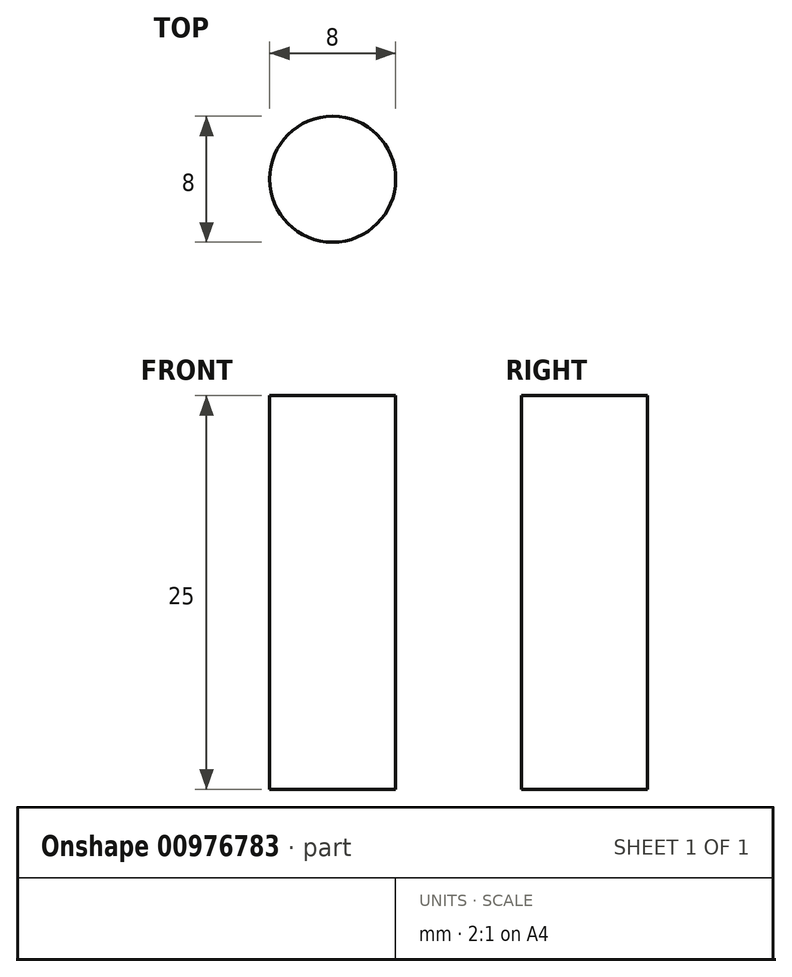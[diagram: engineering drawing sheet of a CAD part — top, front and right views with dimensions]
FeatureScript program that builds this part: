
annotation { "Feature Type Name" : "Feature", "Feature Type Description" : "" }
export const myFeature = defineFeature(function(context is Context, id is Id, definition is map)
    precondition{}
    {
        {
            var Q0;
            Q0=qCreatedBy(makeId("Top.planeOp"),FACE);
            var sketch = newSketch(context, id + "F0", { "sketchPlane" : qUnion([Q0])});
            skCircle(sketch, "E0", {"center": v(0, 0) * mm, "radius": 4 * mm});
            skArc(sketch, "E1", {"start": v(4.61, 14.97) * mm, "mid": v(4.54, 14.95) * mm, "end": v(4.49, 14.9) * mm});
            skArc(sketch, "E2", {"start": v(5.05, 14.83) * mm, "mid": v(4.83, 14.9) * mm, "end": v(4.61, 14.97) * mm});
            skArc(sketch, "E3", {"start": v(5.11, 14.7) * mm, "mid": v(5.1, 14.77) * mm, "end": v(5.05, 14.83) * mm});
            skArc(sketch, "E4", {"start": v(5.1, 14.54) * mm, "mid": v(5.11, 14.62) * mm, "end": v(5.11, 14.7) * mm});
            skArc(sketch, "E5", {"start": v(5.1, 14.54) * mm, "mid": v(5.48, 13.88) * mm, "end": v(6.22, 14.1) * mm});
            skArc(sketch, "E6", {"start": v(6.32, 14.22) * mm, "mid": v(6.27, 14.16) * mm, "end": v(6.22, 14.1) * mm});
            skArc(sketch, "E7", {"start": v(6.45, 14.28) * mm, "mid": v(6.38, 14.26) * mm, "end": v(6.32, 14.22) * mm});
            skArc(sketch, "E8", {"start": v(6.87, 14.08) * mm, "mid": v(6.66, 14.18) * mm, "end": v(6.45, 14.28) * mm});
            skArc(sketch, "E9", {"start": v(6.91, 13.94) * mm, "mid": v(6.9, 14.01) * mm, "end": v(6.87, 14.08) * mm});
            skArc(sketch, "E10", {"start": v(6.89, 13.8) * mm, "mid": v(6.9, 13.86) * mm, "end": v(6.91, 13.94) * mm});
            skArc(sketch, "E11", {"start": v(6.89, 13.8) * mm, "mid": v(7.18, 13.08) * mm, "end": v(7.94, 13.21) * mm});
            skArc(sketch, "E12", {"start": v(8.05, 13.31) * mm, "mid": v(8, 13.27) * mm, "end": v(7.94, 13.21) * mm});
            skArc(sketch, "E13", {"start": v(8.2, 13.36) * mm, "mid": v(8.12, 13.35) * mm, "end": v(8.05, 13.31) * mm});
            skArc(sketch, "E14", {"start": v(8.58, 13.1) * mm, "mid": v(8.39, 13.23) * mm, "end": v(8.2, 13.36) * mm});
            skArc(sketch, "E15", {"start": v(8.6, 12.96) * mm, "mid": v(8.6, 13.04) * mm, "end": v(8.58, 13.1) * mm});
            skArc(sketch, "E16", {"start": v(8.56, 12.82) * mm, "mid": v(8.59, 12.9) * mm, "end": v(8.6, 12.96) * mm});
            skArc(sketch, "E17", {"start": v(8.56, 12.82) * mm, "mid": v(8.76, 12.08) * mm, "end": v(9.53, 12.11) * mm});
            skArc(sketch, "E18", {"start": v(9.66, 12.2) * mm, "mid": v(9.6, 12.16) * mm, "end": v(9.53, 12.11) * mm});
            skArc(sketch, "E19", {"start": v(9.8, 12.22) * mm, "mid": v(9.73, 12.22) * mm, "end": v(9.66, 12.2) * mm});
            skArc(sketch, "E20", {"start": v(10.16, 11.93) * mm, "mid": v(9.98, 12.08) * mm, "end": v(9.8, 12.22) * mm});
            skArc(sketch, "E21", {"start": v(10.16, 11.78) * mm, "mid": v(10.17, 11.86) * mm, "end": v(10.16, 11.93) * mm});
            skArc(sketch, "E22", {"start": v(10.1, 11.64) * mm, "mid": v(10.13, 11.71) * mm, "end": v(10.16, 11.78) * mm});
            skArc(sketch, "E23", {"start": v(10.1, 11.64) * mm, "mid": v(10.2, 10.88) * mm, "end": v(10.98, 10.82) * mm});
            skArc(sketch, "E24", {"start": v(11.1, 10.9) * mm, "mid": v(11.04, 10.86) * mm, "end": v(10.98, 10.82) * mm});
            skArc(sketch, "E25", {"start": v(11.26, 10.9) * mm, "mid": v(11.18, 10.9) * mm, "end": v(11.1, 10.9) * mm});
            skArc(sketch, "E26", {"start": v(11.57, 10.56) * mm, "mid": v(11.42, 10.73) * mm, "end": v(11.26, 10.9) * mm});
            skArc(sketch, "E27", {"start": v(11.56, 10.42) * mm, "mid": v(11.58, 10.49) * mm, "end": v(11.57, 10.56) * mm});
            skArc(sketch, "E28", {"start": v(11.48, 10.29) * mm, "mid": v(11.52, 10.35) * mm, "end": v(11.56, 10.42) * mm});
            skArc(sketch, "E29", {"start": v(11.48, 10.29) * mm, "mid": v(11.5, 9.52) * mm, "end": v(12.24, 9.36) * mm});
            skArc(sketch, "E30", {"start": v(12.39, 9.41) * mm, "mid": v(12.31, 9.4) * mm, "end": v(12.24, 9.36) * mm});
            skArc(sketch, "E31", {"start": v(12.53, 9.4) * mm, "mid": v(12.46, 9.42) * mm, "end": v(12.39, 9.41) * mm});
            skArc(sketch, "E32", {"start": v(12.8, 9.03) * mm, "mid": v(12.67, 9.22) * mm, "end": v(12.53, 9.4) * mm});
            skArc(sketch, "E33", {"start": v(12.77, 8.89) * mm, "mid": v(12.8, 8.95) * mm, "end": v(12.8, 9.03) * mm});
            skArc(sketch, "E34", {"start": v(12.68, 8.77) * mm, "mid": v(12.73, 8.82) * mm, "end": v(12.77, 8.89) * mm});
            skArc(sketch, "E35", {"start": v(12.68, 8.77) * mm, "mid": v(12.6, 8) * mm, "end": v(13.32, 7.75) * mm});
            skArc(sketch, "E36", {"start": v(13.47, 7.79) * mm, "mid": v(13.4, 7.78) * mm, "end": v(13.32, 7.75) * mm});
            skArc(sketch, "E37", {"start": v(13.61, 7.76) * mm, "mid": v(13.54, 7.78) * mm, "end": v(13.47, 7.79) * mm});
            skArc(sketch, "E38", {"start": v(13.84, 7.35) * mm, "mid": v(13.73, 7.56) * mm, "end": v(13.61, 7.76) * mm});
            skArc(sketch, "E39", {"start": v(13.79, 7.22) * mm, "mid": v(13.82, 7.28) * mm, "end": v(13.84, 7.35) * mm});
            skArc(sketch, "E40", {"start": v(13.68, 7.1) * mm, "mid": v(13.73, 7.16) * mm, "end": v(13.79, 7.22) * mm});
            skArc(sketch, "E41", {"start": v(13.68, 7.1) * mm, "mid": v(13.5, 6.36) * mm, "end": v(14.19, 6.02) * mm});
            skArc(sketch, "E42", {"start": v(14.34, 6.04) * mm, "mid": v(14.26, 6.03) * mm, "end": v(14.19, 6.02) * mm});
            skArc(sketch, "E43", {"start": v(14.48, 6) * mm, "mid": v(14.41, 6.03) * mm, "end": v(14.34, 6.04) * mm});
            skArc(sketch, "E44", {"start": v(14.65, 5.56) * mm, "mid": v(14.57, 5.78) * mm, "end": v(14.48, 6) * mm});
            skArc(sketch, "E45", {"start": v(14.58, 5.43) * mm, "mid": v(14.63, 5.49) * mm, "end": v(14.65, 5.56) * mm});
            skArc(sketch, "E46", {"start": v(14.46, 5.34) * mm, "mid": v(14.52, 5.38) * mm, "end": v(14.58, 5.43) * mm});
            skArc(sketch, "E47", {"start": v(14.46, 5.34) * mm, "mid": v(14.19, 4.62) * mm, "end": v(14.83, 4.2) * mm});
            skArc(sketch, "E48", {"start": v(14.98, 4.2) * mm, "mid": v(14.9, 4.2) * mm, "end": v(14.83, 4.2) * mm});
            skArc(sketch, "E49", {"start": v(15.11, 4.13) * mm, "mid": v(15.05, 4.17) * mm, "end": v(14.98, 4.2) * mm});
            skArc(sketch, "E50", {"start": v(15.23, 3.68) * mm, "mid": v(15.17, 3.9) * mm, "end": v(15.11, 4.13) * mm});
            skArc(sketch, "E51", {"start": v(15.15, 3.56) * mm, "mid": v(15.2, 3.61) * mm, "end": v(15.23, 3.68) * mm});
            skArc(sketch, "E52", {"start": v(15.02, 3.48) * mm, "mid": v(15.08, 3.52) * mm, "end": v(15.15, 3.56) * mm});
            skArc(sketch, "E53", {"start": v(15.02, 3.48) * mm, "mid": v(14.65, 2.8) * mm, "end": v(15.24, 2.3) * mm});
            skArc(sketch, "E54", {"start": v(15.4, 2.28) * mm, "mid": v(15.32, 2.3) * mm, "end": v(15.24, 2.3) * mm});
            skArc(sketch, "E55", {"start": v(15.51, 2.2) * mm, "mid": v(15.46, 2.25) * mm, "end": v(15.4, 2.28) * mm});
            skArc(sketch, "E56", {"start": v(15.57, 1.74) * mm, "mid": v(15.54, 1.97) * mm, "end": v(15.51, 2.2) * mm});
            skArc(sketch, "E57", {"start": v(15.47, 1.63) * mm, "mid": v(15.53, 1.68) * mm, "end": v(15.57, 1.74) * mm});
            skArc(sketch, "E58", {"start": v(15.33, 1.57) * mm, "mid": v(15.4, 1.6) * mm, "end": v(15.47, 1.63) * mm});
            skArc(sketch, "E59", {"start": v(15.33, 1.57) * mm, "mid": v(14.89, 0.95) * mm, "end": v(15.4, 0.38) * mm});
            skArc(sketch, "E60", {"start": v(15.56, 0.34) * mm, "mid": v(15.48, 0.36) * mm, "end": v(15.4, 0.38) * mm});
            skArc(sketch, "E61", {"start": v(15.67, 0.24) * mm, "mid": v(15.62, 0.3) * mm, "end": v(15.56, 0.34) * mm});
            skArc(sketch, "E62", {"start": v(15.67, -0.22) * mm, "mid": v(15.67, 0) * mm, "end": v(15.67, 0.24) * mm});
            skArc(sketch, "E63", {"start": v(15.56, -0.32) * mm, "mid": v(15.62, -0.28) * mm, "end": v(15.67, -0.22) * mm});
            skArc(sketch, "E64", {"start": v(15.41, -0.36) * mm, "mid": v(15.48, -0.34) * mm, "end": v(15.56, -0.32) * mm});
            skArc(sketch, "E65", {"start": v(15.41, -0.36) * mm, "mid": v(14.9, -0.93) * mm, "end": v(15.33, -1.56) * mm});
            skArc(sketch, "E66", {"start": v(15.48, -1.62) * mm, "mid": v(15.4, -1.58) * mm, "end": v(15.33, -1.56) * mm});
            skArc(sketch, "E67", {"start": v(15.57, -1.73) * mm, "mid": v(15.53, -1.66) * mm, "end": v(15.48, -1.62) * mm});
            skArc(sketch, "E68", {"start": v(15.52, -2.19) * mm, "mid": v(15.55, -1.96) * mm, "end": v(15.57, -1.73) * mm});
            skArc(sketch, "E69", {"start": v(15.4, -2.27) * mm, "mid": v(15.46, -2.24) * mm, "end": v(15.52, -2.19) * mm});
            skArc(sketch, "E70", {"start": v(15.24, -2.29) * mm, "mid": v(15.32, -2.28) * mm, "end": v(15.4, -2.27) * mm});
            skArc(sketch, "E71", {"start": v(15.24, -2.29) * mm, "mid": v(14.66, -2.79) * mm, "end": v(15.02, -3.47) * mm});
            skArc(sketch, "E72", {"start": v(15.15, -3.54) * mm, "mid": v(15.09, -3.5) * mm, "end": v(15.02, -3.47) * mm});
            skArc(sketch, "E73", {"start": v(15.23, -3.66) * mm, "mid": v(15.2, -3.6) * mm, "end": v(15.15, -3.54) * mm});
            skArc(sketch, "E74", {"start": v(15.12, -4.11) * mm, "mid": v(15.18, -3.89) * mm, "end": v(15.23, -3.66) * mm});
            skArc(sketch, "E75", {"start": v(14.99, -4.18) * mm, "mid": v(15.06, -4.16) * mm, "end": v(15.12, -4.11) * mm});
            skArc(sketch, "E76", {"start": v(14.84, -4.18) * mm, "mid": v(14.91, -4.18) * mm, "end": v(14.99, -4.18) * mm});
            skArc(sketch, "E77", {"start": v(14.84, -4.18) * mm, "mid": v(14.2, -4.6) * mm, "end": v(14.47, -5.32) * mm});
            skArc(sketch, "E78", {"start": v(14.59, -5.41) * mm, "mid": v(14.53, -5.36) * mm, "end": v(14.47, -5.32) * mm});
            skArc(sketch, "E79", {"start": v(14.65, -5.54) * mm, "mid": v(14.63, -5.47) * mm, "end": v(14.59, -5.41) * mm});
            skArc(sketch, "E80", {"start": v(14.48, -5.98) * mm, "mid": v(14.57, -5.76) * mm, "end": v(14.65, -5.54) * mm});
            skArc(sketch, "E81", {"start": v(14.35, -6.02) * mm, "mid": v(14.42, -6.01) * mm, "end": v(14.48, -5.98) * mm});
            skArc(sketch, "E82", {"start": v(14.2, -6) * mm, "mid": v(14.27, -6.02) * mm, "end": v(14.35, -6.02) * mm});
            skArc(sketch, "E83", {"start": v(14.2, -6) * mm, "mid": v(13.5, -6.34) * mm, "end": v(13.68, -7.1) * mm});
            skArc(sketch, "E84", {"start": v(13.8, -7.2) * mm, "mid": v(13.74, -7.14) * mm, "end": v(13.68, -7.1) * mm});
            skArc(sketch, "E85", {"start": v(13.84, -7.34) * mm, "mid": v(13.83, -7.26) * mm, "end": v(13.8, -7.2) * mm});
            skArc(sketch, "E86", {"start": v(13.62, -7.74) * mm, "mid": v(13.73, -7.54) * mm, "end": v(13.84, -7.34) * mm});
            skArc(sketch, "E87", {"start": v(13.48, -7.77) * mm, "mid": v(13.55, -7.77) * mm, "end": v(13.62, -7.74) * mm});
            skArc(sketch, "E88", {"start": v(13.33, -7.74) * mm, "mid": v(13.4, -7.76) * mm, "end": v(13.48, -7.77) * mm});
            skArc(sketch, "E89", {"start": v(13.33, -7.74) * mm, "mid": v(12.6, -7.99) * mm, "end": v(12.69, -8.75) * mm});
            skArc(sketch, "E90", {"start": v(12.78, -8.87) * mm, "mid": v(12.74, -8.8) * mm, "end": v(12.69, -8.75) * mm});
            skArc(sketch, "E91", {"start": v(12.82, -9.01) * mm, "mid": v(12.81, -8.94) * mm, "end": v(12.78, -8.87) * mm});
            skArc(sketch, "E92", {"start": v(12.54, -9.39) * mm, "mid": v(12.68, -9.2) * mm, "end": v(12.82, -9.01) * mm});
            skArc(sketch, "E93", {"start": v(12.4, -9.4) * mm, "mid": v(12.47, -9.4) * mm, "end": v(12.54, -9.39) * mm});
            skArc(sketch, "E94", {"start": v(12.26, -9.35) * mm, "mid": v(12.33, -9.38) * mm, "end": v(12.4, -9.4) * mm});
            skArc(sketch, "E95", {"start": v(12.26, -9.35) * mm, "mid": v(11.5, -9.5) * mm, "end": v(11.5, -10.27) * mm});
            skArc(sketch, "E96", {"start": v(11.57, -10.4) * mm, "mid": v(11.53, -10.34) * mm, "end": v(11.5, -10.27) * mm});
            skArc(sketch, "E97", {"start": v(11.58, -10.55) * mm, "mid": v(11.59, -10.48) * mm, "end": v(11.57, -10.4) * mm});
            skArc(sketch, "E98", {"start": v(11.27, -10.89) * mm, "mid": v(11.43, -10.72) * mm, "end": v(11.58, -10.55) * mm});
            skArc(sketch, "E99", {"start": v(11.12, -10.88) * mm, "mid": v(11.2, -10.9) * mm, "end": v(11.27, -10.89) * mm});
            skArc(sketch, "E100", {"start": v(10.99, -10.81) * mm, "mid": v(11.05, -10.85) * mm, "end": v(11.12, -10.88) * mm});
            skArc(sketch, "E101", {"start": v(10.99, -10.81) * mm, "mid": v(10.22, -10.87) * mm, "end": v(10.11, -11.63) * mm});
            skArc(sketch, "E102", {"start": v(10.17, -11.77) * mm, "mid": v(10.15, -11.7) * mm, "end": v(10.11, -11.63) * mm});
            skArc(sketch, "E103", {"start": v(10.17, -11.92) * mm, "mid": v(10.18, -11.85) * mm, "end": v(10.17, -11.77) * mm});
            skArc(sketch, "E104", {"start": v(9.81, -12.21) * mm, "mid": v(10, -12.07) * mm, "end": v(10.17, -11.92) * mm});
            skArc(sketch, "E105", {"start": v(9.67, -12.19) * mm, "mid": v(9.74, -12.21) * mm, "end": v(9.81, -12.21) * mm});
            skArc(sketch, "E106", {"start": v(9.55, -12.1) * mm, "mid": v(9.6, -12.15) * mm, "end": v(9.67, -12.19) * mm});
            skArc(sketch, "E107", {"start": v(9.55, -12.1) * mm, "mid": v(8.78, -12.07) * mm, "end": v(8.57, -12.8) * mm});
            skArc(sketch, "E108", {"start": v(8.62, -12.95) * mm, "mid": v(8.6, -12.88) * mm, "end": v(8.57, -12.8) * mm});
            skArc(sketch, "E109", {"start": v(8.6, -13.1) * mm, "mid": v(8.62, -13.03) * mm, "end": v(8.62, -12.95) * mm});
            skArc(sketch, "E110", {"start": v(8.2, -13.35) * mm, "mid": v(8.4, -13.22) * mm, "end": v(8.6, -13.1) * mm});
            skArc(sketch, "E111", {"start": v(8.07, -13.3) * mm, "mid": v(8.13, -13.34) * mm, "end": v(8.2, -13.35) * mm});
            skArc(sketch, "E112", {"start": v(7.95, -13.2) * mm, "mid": v(8, -13.26) * mm, "end": v(8.07, -13.3) * mm});
            skArc(sketch, "E113", {"start": v(7.95, -13.2) * mm, "mid": v(7.2, -13.07) * mm, "end": v(6.9, -13.78) * mm});
            skArc(sketch, "E114", {"start": v(6.93, -13.93) * mm, "mid": v(6.92, -13.86) * mm, "end": v(6.9, -13.78) * mm});
            skArc(sketch, "E115", {"start": v(6.89, -14.07) * mm, "mid": v(6.92, -14) * mm, "end": v(6.93, -13.93) * mm});
            skArc(sketch, "E116", {"start": v(6.47, -14.27) * mm, "mid": v(6.68, -14.17) * mm, "end": v(6.89, -14.07) * mm});
            skArc(sketch, "E117", {"start": v(6.34, -14.21) * mm, "mid": v(6.4, -14.25) * mm, "end": v(6.47, -14.27) * mm});
            skArc(sketch, "E118", {"start": v(6.24, -14.1) * mm, "mid": v(6.28, -14.16) * mm, "end": v(6.34, -14.21) * mm});
            skArc(sketch, "E119", {"start": v(6.24, -14.1) * mm, "mid": v(5.5, -13.87) * mm, "end": v(5.12, -14.54) * mm});
            skArc(sketch, "E120", {"start": v(5.13, -14.7) * mm, "mid": v(5.13, -14.61) * mm, "end": v(5.12, -14.54) * mm});
            skArc(sketch, "E121", {"start": v(5.07, -14.83) * mm, "mid": v(5.1, -14.76) * mm, "end": v(5.13, -14.7) * mm});
            skArc(sketch, "E122", {"start": v(4.63, -14.97) * mm, "mid": v(4.85, -14.9) * mm, "end": v(5.07, -14.83) * mm});
            skArc(sketch, "E123", {"start": v(4.5, -14.9) * mm, "mid": v(4.56, -14.94) * mm, "end": v(4.63, -14.97) * mm});
            skArc(sketch, "E124", {"start": v(4.42, -14.77) * mm, "mid": v(4.46, -14.83) * mm, "end": v(4.5, -14.9) * mm});
            skArc(sketch, "E125", {"start": v(4.42, -14.77) * mm, "mid": v(3.72, -14.45) * mm, "end": v(3.26, -15.07) * mm});
            skArc(sketch, "E126", {"start": v(3.24, -15.22) * mm, "mid": v(3.26, -15.14) * mm, "end": v(3.26, -15.07) * mm});
            skArc(sketch, "E127", {"start": v(3.17, -15.34) * mm, "mid": v(3.22, -15.29) * mm, "end": v(3.24, -15.22) * mm});
            skArc(sketch, "E128", {"start": v(2.72, -15.43) * mm, "mid": v(2.94, -15.39) * mm, "end": v(3.17, -15.34) * mm});
            skArc(sketch, "E129", {"start": v(2.6, -15.34) * mm, "mid": v(2.65, -15.4) * mm, "end": v(2.72, -15.43) * mm});
            skArc(sketch, "E130", {"start": v(2.53, -15.2) * mm, "mid": v(2.56, -15.27) * mm, "end": v(2.6, -15.34) * mm});
            skArc(sketch, "E131", {"start": v(2.53, -15.2) * mm, "mid": v(1.88, -14.8) * mm, "end": v(1.34, -15.35) * mm});
            skArc(sketch, "E132", {"start": v(1.31, -15.5) * mm, "mid": v(1.33, -15.43) * mm, "end": v(1.34, -15.35) * mm});
            skArc(sketch, "E133", {"start": v(1.22, -15.62) * mm, "mid": v(1.28, -15.57) * mm, "end": v(1.31, -15.5) * mm});
            skArc(sketch, "E134", {"start": v(0.76, -15.65) * mm, "mid": v(1, -15.64) * mm, "end": v(1.22, -15.62) * mm});
            skArc(sketch, "E135", {"start": v(0.66, -15.55) * mm, "mid": v(0.7, -15.6) * mm, "end": v(0.76, -15.65) * mm});
            skArc(sketch, "E136", {"start": v(0.6, -15.4) * mm, "mid": v(0.63, -15.48) * mm, "end": v(0.66, -15.55) * mm});
            skArc(sketch, "E137", {"start": v(0.6, -15.4) * mm, "mid": v(0, -14.92) * mm, "end": v(-0.6, -15.4) * mm});
            skArc(sketch, "E138", {"start": v(-0.64, -15.55) * mm, "mid": v(-0.61, -15.48) * mm, "end": v(-0.6, -15.4) * mm});
            skArc(sketch, "E139", {"start": v(-0.74, -15.65) * mm, "mid": v(-0.68, -15.6) * mm, "end": v(-0.64, -15.55) * mm});
            skArc(sketch, "E140", {"start": v(-1.2, -15.62) * mm, "mid": v(-0.98, -15.64) * mm, "end": v(-0.74, -15.65) * mm});
            skArc(sketch, "E141", {"start": v(-1.3, -15.5) * mm, "mid": v(-1.26, -15.57) * mm, "end": v(-1.2, -15.62) * mm});
            skArc(sketch, "E142", {"start": v(-1.33, -15.36) * mm, "mid": v(-1.32, -15.43) * mm, "end": v(-1.3, -15.5) * mm});
            skArc(sketch, "E143", {"start": v(-1.33, -15.36) * mm, "mid": v(-1.86, -14.8) * mm, "end": v(-2.52, -15.2) * mm});
            skArc(sketch, "E144", {"start": v(-2.59, -15.34) * mm, "mid": v(-2.55, -15.28) * mm, "end": v(-2.52, -15.2) * mm});
            skArc(sketch, "E145", {"start": v(-2.7, -15.43) * mm, "mid": v(-2.64, -15.4) * mm, "end": v(-2.59, -15.34) * mm});
            skArc(sketch, "E146", {"start": v(-3.16, -15.35) * mm, "mid": v(-2.93, -15.4) * mm, "end": v(-2.7, -15.43) * mm});
            skArc(sketch, "E147", {"start": v(-3.23, -15.22) * mm, "mid": v(-3.2, -15.3) * mm, "end": v(-3.16, -15.35) * mm});
            skArc(sketch, "E148", {"start": v(-3.24, -15.07) * mm, "mid": v(-3.24, -15.15) * mm, "end": v(-3.23, -15.22) * mm});
            skArc(sketch, "E149", {"start": v(-3.24, -15.07) * mm, "mid": v(-3.7, -14.45) * mm, "end": v(-4.4, -14.77) * mm});
            skArc(sketch, "E150", {"start": v(-4.49, -14.9) * mm, "mid": v(-4.44, -14.84) * mm, "end": v(-4.4, -14.77) * mm});
            skArc(sketch, "E151", {"start": v(-4.61, -14.97) * mm, "mid": v(-4.54, -14.95) * mm, "end": v(-4.49, -14.9) * mm});
            skArc(sketch, "E152", {"start": v(-5.05, -14.83) * mm, "mid": v(-4.83, -14.9) * mm, "end": v(-4.61, -14.97) * mm});
            skArc(sketch, "E153", {"start": v(-5.11, -14.7) * mm, "mid": v(-5.1, -14.77) * mm, "end": v(-5.05, -14.83) * mm});
            skArc(sketch, "E154", {"start": v(-5.1, -14.54) * mm, "mid": v(-5.11, -14.62) * mm, "end": v(-5.11, -14.7) * mm});
            skArc(sketch, "E155", {"start": v(-5.1, -14.54) * mm, "mid": v(-5.48, -13.88) * mm, "end": v(-6.22, -14.1) * mm});
            skArc(sketch, "E156", {"start": v(-6.32, -14.22) * mm, "mid": v(-6.27, -14.16) * mm, "end": v(-6.22, -14.1) * mm});
            skArc(sketch, "E157", {"start": v(-6.45, -14.28) * mm, "mid": v(-6.38, -14.26) * mm, "end": v(-6.32, -14.22) * mm});
            skArc(sketch, "E158", {"start": v(-6.87, -14.08) * mm, "mid": v(-6.66, -14.18) * mm, "end": v(-6.45, -14.28) * mm});
            skArc(sketch, "E159", {"start": v(-6.91, -13.94) * mm, "mid": v(-6.9, -14.01) * mm, "end": v(-6.87, -14.08) * mm});
            skArc(sketch, "E160", {"start": v(-6.89, -13.8) * mm, "mid": v(-6.9, -13.86) * mm, "end": v(-6.91, -13.94) * mm});
            skArc(sketch, "E161", {"start": v(-6.89, -13.8) * mm, "mid": v(-7.18, -13.08) * mm, "end": v(-7.94, -13.21) * mm});
            skArc(sketch, "E162", {"start": v(-8.05, -13.31) * mm, "mid": v(-8, -13.27) * mm, "end": v(-7.94, -13.21) * mm});
            skArc(sketch, "E163", {"start": v(-8.2, -13.36) * mm, "mid": v(-8.12, -13.35) * mm, "end": v(-8.05, -13.31) * mm});
            skArc(sketch, "E164", {"start": v(-8.58, -13.1) * mm, "mid": v(-8.39, -13.23) * mm, "end": v(-8.2, -13.36) * mm});
            skArc(sketch, "E165", {"start": v(-8.6, -12.96) * mm, "mid": v(-8.6, -13.04) * mm, "end": v(-8.58, -13.1) * mm});
            skArc(sketch, "E166", {"start": v(-8.56, -12.82) * mm, "mid": v(-8.59, -12.9) * mm, "end": v(-8.6, -12.96) * mm});
            skArc(sketch, "E167", {"start": v(-8.56, -12.82) * mm, "mid": v(-8.76, -12.08) * mm, "end": v(-9.53, -12.11) * mm});
            skArc(sketch, "E168", {"start": v(-9.66, -12.2) * mm, "mid": v(-9.6, -12.16) * mm, "end": v(-9.53, -12.11) * mm});
            skArc(sketch, "E169", {"start": v(-9.8, -12.22) * mm, "mid": v(-9.73, -12.22) * mm, "end": v(-9.66, -12.2) * mm});
            skArc(sketch, "E170", {"start": v(-10.16, -11.93) * mm, "mid": v(-9.98, -12.08) * mm, "end": v(-9.8, -12.22) * mm});
            skArc(sketch, "E171", {"start": v(-10.16, -11.78) * mm, "mid": v(-10.17, -11.86) * mm, "end": v(-10.16, -11.93) * mm});
            skArc(sketch, "E172", {"start": v(-10.1, -11.64) * mm, "mid": v(-10.13, -11.71) * mm, "end": v(-10.16, -11.78) * mm});
            skArc(sketch, "E173", {"start": v(-10.1, -11.64) * mm, "mid": v(-10.2, -10.88) * mm, "end": v(-10.98, -10.82) * mm});
            skArc(sketch, "E174", {"start": v(-11.1, -10.9) * mm, "mid": v(-11.04, -10.86) * mm, "end": v(-10.98, -10.82) * mm});
            skArc(sketch, "E175", {"start": v(-11.26, -10.9) * mm, "mid": v(-11.18, -10.9) * mm, "end": v(-11.1, -10.9) * mm});
            skArc(sketch, "E176", {"start": v(-11.57, -10.56) * mm, "mid": v(-11.42, -10.73) * mm, "end": v(-11.26, -10.9) * mm});
            skArc(sketch, "E177", {"start": v(-11.56, -10.42) * mm, "mid": v(-11.58, -10.49) * mm, "end": v(-11.57, -10.56) * mm});
            skArc(sketch, "E178", {"start": v(-11.48, -10.29) * mm, "mid": v(-11.52, -10.35) * mm, "end": v(-11.56, -10.42) * mm});
            skArc(sketch, "E179", {"start": v(-11.48, -10.29) * mm, "mid": v(-11.5, -9.52) * mm, "end": v(-12.24, -9.36) * mm});
            skArc(sketch, "E180", {"start": v(-12.39, -9.41) * mm, "mid": v(-12.31, -9.4) * mm, "end": v(-12.24, -9.36) * mm});
            skArc(sketch, "E181", {"start": v(-12.53, -9.4) * mm, "mid": v(-12.46, -9.42) * mm, "end": v(-12.39, -9.41) * mm});
            skArc(sketch, "E182", {"start": v(-12.8, -9.03) * mm, "mid": v(-12.67, -9.22) * mm, "end": v(-12.53, -9.4) * mm});
            skArc(sketch, "E183", {"start": v(-12.77, -8.89) * mm, "mid": v(-12.8, -8.95) * mm, "end": v(-12.8, -9.03) * mm});
            skArc(sketch, "E184", {"start": v(-12.68, -8.77) * mm, "mid": v(-12.73, -8.82) * mm, "end": v(-12.77, -8.89) * mm});
            skArc(sketch, "E185", {"start": v(-12.68, -8.77) * mm, "mid": v(-12.6, -8) * mm, "end": v(-13.32, -7.75) * mm});
            skArc(sketch, "E186", {"start": v(-13.47, -7.79) * mm, "mid": v(-13.4, -7.78) * mm, "end": v(-13.32, -7.75) * mm});
            skArc(sketch, "E187", {"start": v(-13.61, -7.76) * mm, "mid": v(-13.54, -7.78) * mm, "end": v(-13.47, -7.79) * mm});
            skArc(sketch, "E188", {"start": v(-13.84, -7.35) * mm, "mid": v(-13.73, -7.56) * mm, "end": v(-13.61, -7.76) * mm});
            skArc(sketch, "E189", {"start": v(-13.79, -7.22) * mm, "mid": v(-13.82, -7.28) * mm, "end": v(-13.84, -7.35) * mm});
            skArc(sketch, "E190", {"start": v(-13.68, -7.1) * mm, "mid": v(-13.73, -7.16) * mm, "end": v(-13.79, -7.22) * mm});
            skArc(sketch, "E191", {"start": v(-13.68, -7.1) * mm, "mid": v(-13.5, -6.36) * mm, "end": v(-14.19, -6.02) * mm});
            skArc(sketch, "E192", {"start": v(-14.34, -6.04) * mm, "mid": v(-14.26, -6.03) * mm, "end": v(-14.19, -6.02) * mm});
            skArc(sketch, "E193", {"start": v(-14.48, -6) * mm, "mid": v(-14.41, -6.03) * mm, "end": v(-14.34, -6.04) * mm});
            skArc(sketch, "E194", {"start": v(-14.65, -5.56) * mm, "mid": v(-14.57, -5.78) * mm, "end": v(-14.48, -6) * mm});
            skArc(sketch, "E195", {"start": v(-14.58, -5.43) * mm, "mid": v(-14.63, -5.49) * mm, "end": v(-14.65, -5.56) * mm});
            skArc(sketch, "E196", {"start": v(-14.46, -5.34) * mm, "mid": v(-14.52, -5.38) * mm, "end": v(-14.58, -5.43) * mm});
            skArc(sketch, "E197", {"start": v(-14.46, -5.34) * mm, "mid": v(-14.19, -4.62) * mm, "end": v(-14.83, -4.2) * mm});
            skArc(sketch, "E198", {"start": v(-14.98, -4.2) * mm, "mid": v(-14.9, -4.2) * mm, "end": v(-14.83, -4.2) * mm});
            skArc(sketch, "E199", {"start": v(-15.11, -4.13) * mm, "mid": v(-15.05, -4.17) * mm, "end": v(-14.98, -4.2) * mm});
            skArc(sketch, "E200", {"start": v(-15.23, -3.68) * mm, "mid": v(-15.17, -3.9) * mm, "end": v(-15.11, -4.13) * mm});
            skArc(sketch, "E201", {"start": v(-15.15, -3.56) * mm, "mid": v(-15.2, -3.61) * mm, "end": v(-15.23, -3.68) * mm});
            skArc(sketch, "E202", {"start": v(-15.02, -3.48) * mm, "mid": v(-15.08, -3.52) * mm, "end": v(-15.15, -3.56) * mm});
            skArc(sketch, "E203", {"start": v(-15.02, -3.48) * mm, "mid": v(-14.65, -2.8) * mm, "end": v(-15.24, -2.3) * mm});
            skArc(sketch, "E204", {"start": v(-15.4, -2.28) * mm, "mid": v(-15.32, -2.3) * mm, "end": v(-15.24, -2.3) * mm});
            skArc(sketch, "E205", {"start": v(-15.51, -2.2) * mm, "mid": v(-15.46, -2.25) * mm, "end": v(-15.4, -2.28) * mm});
            skArc(sketch, "E206", {"start": v(-15.57, -1.74) * mm, "mid": v(-15.54, -1.97) * mm, "end": v(-15.51, -2.2) * mm});
            skArc(sketch, "E207", {"start": v(-15.47, -1.63) * mm, "mid": v(-15.53, -1.68) * mm, "end": v(-15.57, -1.74) * mm});
            skArc(sketch, "E208", {"start": v(-15.33, -1.57) * mm, "mid": v(-15.4, -1.6) * mm, "end": v(-15.47, -1.63) * mm});
            skArc(sketch, "E209", {"start": v(-15.33, -1.57) * mm, "mid": v(-14.89, -0.95) * mm, "end": v(-15.4, -0.38) * mm});
            skArc(sketch, "E210", {"start": v(-15.56, -0.34) * mm, "mid": v(-15.48, -0.36) * mm, "end": v(-15.4, -0.38) * mm});
            skArc(sketch, "E211", {"start": v(-15.67, -0.24) * mm, "mid": v(-15.62, -0.3) * mm, "end": v(-15.56, -0.34) * mm});
            skArc(sketch, "E212", {"start": v(-15.67, 0.22) * mm, "mid": v(-15.67, 0) * mm, "end": v(-15.67, -0.24) * mm});
            skArc(sketch, "E213", {"start": v(-15.56, 0.32) * mm, "mid": v(-15.62, 0.28) * mm, "end": v(-15.67, 0.22) * mm});
            skArc(sketch, "E214", {"start": v(-15.41, 0.36) * mm, "mid": v(-15.48, 0.34) * mm, "end": v(-15.56, 0.32) * mm});
            skArc(sketch, "E215", {"start": v(-15.41, 0.36) * mm, "mid": v(-14.9, 0.93) * mm, "end": v(-15.33, 1.56) * mm});
            skArc(sketch, "E216", {"start": v(-15.48, 1.62) * mm, "mid": v(-15.4, 1.58) * mm, "end": v(-15.33, 1.56) * mm});
            skArc(sketch, "E217", {"start": v(-15.57, 1.73) * mm, "mid": v(-15.53, 1.66) * mm, "end": v(-15.48, 1.62) * mm});
            skArc(sketch, "E218", {"start": v(-15.52, 2.19) * mm, "mid": v(-15.55, 1.96) * mm, "end": v(-15.57, 1.73) * mm});
            skArc(sketch, "E219", {"start": v(-15.4, 2.27) * mm, "mid": v(-15.46, 2.24) * mm, "end": v(-15.52, 2.19) * mm});
            skArc(sketch, "E220", {"start": v(-15.24, 2.29) * mm, "mid": v(-15.32, 2.28) * mm, "end": v(-15.4, 2.27) * mm});
            skArc(sketch, "E221", {"start": v(-15.24, 2.29) * mm, "mid": v(-14.66, 2.79) * mm, "end": v(-15.02, 3.47) * mm});
            skArc(sketch, "E222", {"start": v(-15.15, 3.54) * mm, "mid": v(-15.09, 3.5) * mm, "end": v(-15.02, 3.47) * mm});
            skArc(sketch, "E223", {"start": v(-15.23, 3.66) * mm, "mid": v(-15.2, 3.6) * mm, "end": v(-15.15, 3.54) * mm});
            skArc(sketch, "E224", {"start": v(-15.12, 4.11) * mm, "mid": v(-15.18, 3.89) * mm, "end": v(-15.23, 3.66) * mm});
            skArc(sketch, "E225", {"start": v(-14.99, 4.18) * mm, "mid": v(-15.06, 4.16) * mm, "end": v(-15.12, 4.11) * mm});
            skArc(sketch, "E226", {"start": v(-14.84, 4.18) * mm, "mid": v(-14.91, 4.18) * mm, "end": v(-14.99, 4.18) * mm});
            skArc(sketch, "E227", {"start": v(-14.84, 4.18) * mm, "mid": v(-14.2, 4.6) * mm, "end": v(-14.47, 5.32) * mm});
            skArc(sketch, "E228", {"start": v(-14.59, 5.41) * mm, "mid": v(-14.53, 5.36) * mm, "end": v(-14.47, 5.32) * mm});
            skArc(sketch, "E229", {"start": v(-14.65, 5.54) * mm, "mid": v(-14.63, 5.47) * mm, "end": v(-14.59, 5.41) * mm});
            skArc(sketch, "E230", {"start": v(-14.48, 5.98) * mm, "mid": v(-14.57, 5.76) * mm, "end": v(-14.65, 5.54) * mm});
            skArc(sketch, "E231", {"start": v(-14.35, 6.02) * mm, "mid": v(-14.42, 6.01) * mm, "end": v(-14.48, 5.98) * mm});
            skArc(sketch, "E232", {"start": v(-14.2, 6) * mm, "mid": v(-14.27, 6.02) * mm, "end": v(-14.35, 6.02) * mm});
            skArc(sketch, "E233", {"start": v(-14.2, 6) * mm, "mid": v(-13.5, 6.34) * mm, "end": v(-13.68, 7.1) * mm});
            skArc(sketch, "E234", {"start": v(-13.8, 7.2) * mm, "mid": v(-13.74, 7.14) * mm, "end": v(-13.68, 7.1) * mm});
            skArc(sketch, "E235", {"start": v(-13.84, 7.34) * mm, "mid": v(-13.83, 7.26) * mm, "end": v(-13.8, 7.2) * mm});
            skArc(sketch, "E236", {"start": v(-13.62, 7.74) * mm, "mid": v(-13.73, 7.54) * mm, "end": v(-13.84, 7.34) * mm});
            skArc(sketch, "E237", {"start": v(-13.48, 7.77) * mm, "mid": v(-13.55, 7.77) * mm, "end": v(-13.62, 7.74) * mm});
            skArc(sketch, "E238", {"start": v(-13.33, 7.74) * mm, "mid": v(-13.4, 7.76) * mm, "end": v(-13.48, 7.77) * mm});
            skArc(sketch, "E239", {"start": v(-13.33, 7.74) * mm, "mid": v(-12.6, 7.99) * mm, "end": v(-12.69, 8.75) * mm});
            skArc(sketch, "E240", {"start": v(-12.78, 8.87) * mm, "mid": v(-12.74, 8.8) * mm, "end": v(-12.69, 8.75) * mm});
            skArc(sketch, "E241", {"start": v(-12.82, 9.01) * mm, "mid": v(-12.81, 8.94) * mm, "end": v(-12.78, 8.87) * mm});
            skArc(sketch, "E242", {"start": v(-12.54, 9.39) * mm, "mid": v(-12.68, 9.2) * mm, "end": v(-12.82, 9.01) * mm});
            skArc(sketch, "E243", {"start": v(-12.4, 9.4) * mm, "mid": v(-12.47, 9.4) * mm, "end": v(-12.54, 9.39) * mm});
            skArc(sketch, "E244", {"start": v(-12.26, 9.35) * mm, "mid": v(-12.33, 9.38) * mm, "end": v(-12.4, 9.4) * mm});
            skArc(sketch, "E245", {"start": v(-12.26, 9.35) * mm, "mid": v(-11.5, 9.5) * mm, "end": v(-11.5, 10.27) * mm});
            skArc(sketch, "E246", {"start": v(-11.57, 10.4) * mm, "mid": v(-11.53, 10.34) * mm, "end": v(-11.5, 10.27) * mm});
            skArc(sketch, "E247", {"start": v(-11.58, 10.55) * mm, "mid": v(-11.59, 10.48) * mm, "end": v(-11.57, 10.4) * mm});
            skArc(sketch, "E248", {"start": v(-11.27, 10.89) * mm, "mid": v(-11.43, 10.72) * mm, "end": v(-11.58, 10.55) * mm});
            skArc(sketch, "E249", {"start": v(-11.12, 10.88) * mm, "mid": v(-11.2, 10.9) * mm, "end": v(-11.27, 10.89) * mm});
            skArc(sketch, "E250", {"start": v(-10.99, 10.81) * mm, "mid": v(-11.05, 10.85) * mm, "end": v(-11.12, 10.88) * mm});
            skArc(sketch, "E251", {"start": v(-10.99, 10.81) * mm, "mid": v(-10.22, 10.87) * mm, "end": v(-10.11, 11.63) * mm});
            skArc(sketch, "E252", {"start": v(-10.17, 11.77) * mm, "mid": v(-10.15, 11.7) * mm, "end": v(-10.11, 11.63) * mm});
            skArc(sketch, "E253", {"start": v(-10.17, 11.92) * mm, "mid": v(-10.18, 11.85) * mm, "end": v(-10.17, 11.77) * mm});
            skArc(sketch, "E254", {"start": v(-9.81, 12.21) * mm, "mid": v(-10, 12.07) * mm, "end": v(-10.17, 11.92) * mm});
            skArc(sketch, "E255", {"start": v(-9.67, 12.19) * mm, "mid": v(-9.74, 12.21) * mm, "end": v(-9.81, 12.21) * mm});
            skArc(sketch, "E256", {"start": v(-9.55, 12.1) * mm, "mid": v(-9.6, 12.15) * mm, "end": v(-9.67, 12.19) * mm});
            skArc(sketch, "E257", {"start": v(-9.55, 12.1) * mm, "mid": v(-8.78, 12.07) * mm, "end": v(-8.57, 12.8) * mm});
            skArc(sketch, "E258", {"start": v(-8.62, 12.95) * mm, "mid": v(-8.6, 12.88) * mm, "end": v(-8.57, 12.8) * mm});
            skArc(sketch, "E259", {"start": v(-8.6, 13.1) * mm, "mid": v(-8.62, 13.03) * mm, "end": v(-8.62, 12.95) * mm});
            skArc(sketch, "E260", {"start": v(-8.2, 13.35) * mm, "mid": v(-8.4, 13.22) * mm, "end": v(-8.6, 13.1) * mm});
            skArc(sketch, "E261", {"start": v(-8.07, 13.3) * mm, "mid": v(-8.13, 13.34) * mm, "end": v(-8.2, 13.35) * mm});
            skArc(sketch, "E262", {"start": v(-7.95, 13.2) * mm, "mid": v(-8, 13.26) * mm, "end": v(-8.07, 13.3) * mm});
            skArc(sketch, "E263", {"start": v(-7.95, 13.2) * mm, "mid": v(-7.2, 13.07) * mm, "end": v(-6.9, 13.78) * mm});
            skArc(sketch, "E264", {"start": v(-6.93, 13.93) * mm, "mid": v(-6.92, 13.86) * mm, "end": v(-6.9, 13.78) * mm});
            skArc(sketch, "E265", {"start": v(-6.89, 14.07) * mm, "mid": v(-6.92, 14) * mm, "end": v(-6.93, 13.93) * mm});
            skArc(sketch, "E266", {"start": v(-6.47, 14.27) * mm, "mid": v(-6.68, 14.17) * mm, "end": v(-6.89, 14.07) * mm});
            skArc(sketch, "E267", {"start": v(-6.34, 14.21) * mm, "mid": v(-6.4, 14.25) * mm, "end": v(-6.47, 14.27) * mm});
            skArc(sketch, "E268", {"start": v(-6.24, 14.1) * mm, "mid": v(-6.28, 14.16) * mm, "end": v(-6.34, 14.21) * mm});
            skArc(sketch, "E269", {"start": v(-6.24, 14.1) * mm, "mid": v(-5.5, 13.87) * mm, "end": v(-5.12, 14.54) * mm});
            skArc(sketch, "E270", {"start": v(-5.13, 14.7) * mm, "mid": v(-5.13, 14.61) * mm, "end": v(-5.12, 14.54) * mm});
            skArc(sketch, "E271", {"start": v(-5.07, 14.83) * mm, "mid": v(-5.1, 14.76) * mm, "end": v(-5.13, 14.7) * mm});
            skArc(sketch, "E272", {"start": v(-4.63, 14.97) * mm, "mid": v(-4.85, 14.9) * mm, "end": v(-5.07, 14.83) * mm});
            skArc(sketch, "E273", {"start": v(-4.5, 14.9) * mm, "mid": v(-4.56, 14.94) * mm, "end": v(-4.63, 14.97) * mm});
            skArc(sketch, "E274", {"start": v(-4.42, 14.77) * mm, "mid": v(-4.46, 14.83) * mm, "end": v(-4.5, 14.9) * mm});
            skArc(sketch, "E275", {"start": v(-4.42, 14.77) * mm, "mid": v(-3.72, 14.45) * mm, "end": v(-3.26, 15.07) * mm});
            skArc(sketch, "E276", {"start": v(-3.24, 15.22) * mm, "mid": v(-3.26, 15.14) * mm, "end": v(-3.26, 15.07) * mm});
            skArc(sketch, "E277", {"start": v(-3.17, 15.34) * mm, "mid": v(-3.22, 15.29) * mm, "end": v(-3.24, 15.22) * mm});
            skArc(sketch, "E278", {"start": v(-2.72, 15.43) * mm, "mid": v(-2.94, 15.39) * mm, "end": v(-3.17, 15.34) * mm});
            skArc(sketch, "E279", {"start": v(-2.6, 15.34) * mm, "mid": v(-2.65, 15.4) * mm, "end": v(-2.72, 15.43) * mm});
            skArc(sketch, "E280", {"start": v(-2.53, 15.2) * mm, "mid": v(-2.56, 15.27) * mm, "end": v(-2.6, 15.34) * mm});
            skArc(sketch, "E281", {"start": v(-2.53, 15.2) * mm, "mid": v(-1.88, 14.8) * mm, "end": v(-1.34, 15.35) * mm});
            skArc(sketch, "E282", {"start": v(-1.31, 15.5) * mm, "mid": v(-1.33, 15.43) * mm, "end": v(-1.34, 15.35) * mm});
            skArc(sketch, "E283", {"start": v(-1.22, 15.62) * mm, "mid": v(-1.28, 15.57) * mm, "end": v(-1.31, 15.5) * mm});
            skArc(sketch, "E284", {"start": v(-0.76, 15.65) * mm, "mid": v(-1, 15.64) * mm, "end": v(-1.22, 15.62) * mm});
            skArc(sketch, "E285", {"start": v(-0.66, 15.55) * mm, "mid": v(-0.7, 15.6) * mm, "end": v(-0.76, 15.65) * mm});
            skArc(sketch, "E286", {"start": v(-0.6, 15.4) * mm, "mid": v(-0.63, 15.48) * mm, "end": v(-0.66, 15.55) * mm});
            skArc(sketch, "E287", {"start": v(-0.6, 15.4) * mm, "mid": v(0, 14.92) * mm, "end": v(0.6, 15.4) * mm});
            skArc(sketch, "E288", {"start": v(0.64, 15.55) * mm, "mid": v(0.61, 15.48) * mm, "end": v(0.6, 15.4) * mm});
            skArc(sketch, "E289", {"start": v(0.74, 15.65) * mm, "mid": v(0.68, 15.6) * mm, "end": v(0.64, 15.55) * mm});
            skArc(sketch, "E290", {"start": v(1.2, 15.62) * mm, "mid": v(0.98, 15.64) * mm, "end": v(0.74, 15.65) * mm});
            skArc(sketch, "E291", {"start": v(1.3, 15.5) * mm, "mid": v(1.26, 15.57) * mm, "end": v(1.2, 15.62) * mm});
            skArc(sketch, "E292", {"start": v(1.33, 15.36) * mm, "mid": v(1.32, 15.43) * mm, "end": v(1.3, 15.5) * mm});
            skArc(sketch, "E293", {"start": v(1.33, 15.36) * mm, "mid": v(1.86, 14.8) * mm, "end": v(2.52, 15.2) * mm});
            skArc(sketch, "E294", {"start": v(2.59, 15.34) * mm, "mid": v(2.55, 15.28) * mm, "end": v(2.52, 15.2) * mm});
            skArc(sketch, "E295", {"start": v(2.7, 15.43) * mm, "mid": v(2.64, 15.4) * mm, "end": v(2.59, 15.34) * mm});
            skArc(sketch, "E296", {"start": v(3.16, 15.35) * mm, "mid": v(2.93, 15.4) * mm, "end": v(2.7, 15.43) * mm});
            skArc(sketch, "E297", {"start": v(3.23, 15.22) * mm, "mid": v(3.2, 15.3) * mm, "end": v(3.16, 15.35) * mm});
            skArc(sketch, "E298", {"start": v(3.24, 15.07) * mm, "mid": v(3.24, 15.15) * mm, "end": v(3.23, 15.22) * mm});
            skArc(sketch, "E299", {"start": v(3.24, 15.07) * mm, "mid": v(3.7, 14.45) * mm, "end": v(4.4, 14.77) * mm});
            skArc(sketch, "E300", {"start": v(4.49, 14.9) * mm, "mid": v(4.44, 14.84) * mm, "end": v(4.4, 14.77) * mm});
            skSolve(sketch);
        }
        {
            var Q0;
            Q0=makeQuery(id+"F0.imprint","IMPRINT",FACE,{"disambiguationData":[TD([[makeQuery(id+"F0.imprint","IMPRINT",EDGE,{"derivedFrom":sQuery(id+"F0.wireOp",EDGE,"E0")}),1.0]])]});
            extrude(context, id + "F1", {"entities" : qUnion([Q0]), "depth" : 25 * mm, "offsetDistance" : 25 * mm});
        }
    });
